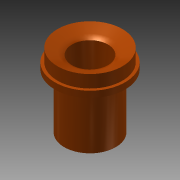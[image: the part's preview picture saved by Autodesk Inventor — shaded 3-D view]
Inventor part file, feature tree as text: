
AUTODESK INVENTOR PART (.ipt)
format: ipt  version: 2015 (Build 190159000, 159)  size: 150,016 bytes
history: native  units: in
note: dims shown in document units (in); Inventor stores cm internally (conversion verified against a paired STEP export)
features: revolve x1, sketch x1
ambient origin geometry x8: Origin, YZ Plane, XZ Plane, XY Plane, X Axis, Y Axis, Z Axis, Center Point
bodies: Solid1 (feature_tree)
feature tree (2):
  revolve  "Revolution1"  [1 undecoded]
  sketch  "Sketch1"  dims[d25=90.0deg d56=0.75in d57=1.0in d58=0.2185in d59=2.594in d60=0.5841in d61=0.5in d62=0.5in d63=1.75in d64=0.25in d65=105.0deg d66=0.5in d67=0.5in d68=0.25in d69=0.375in d70=2.0in d71=0.5in d72=0.25in d73=0.234in d74=0.25in d75=2.0in d76=0.25in d77=105.0deg d78=0.125in d79=0.25in d80=2.3995in d81=0.125in d82=0.25in d83=1.0in d84=1.6531in d85=0.1443in]
note: 1 required parameter value undecoded (feature->parameter linkage not recoverable at this tier; creation-order binding heuristic only, values carry confidence <= 0.55)
